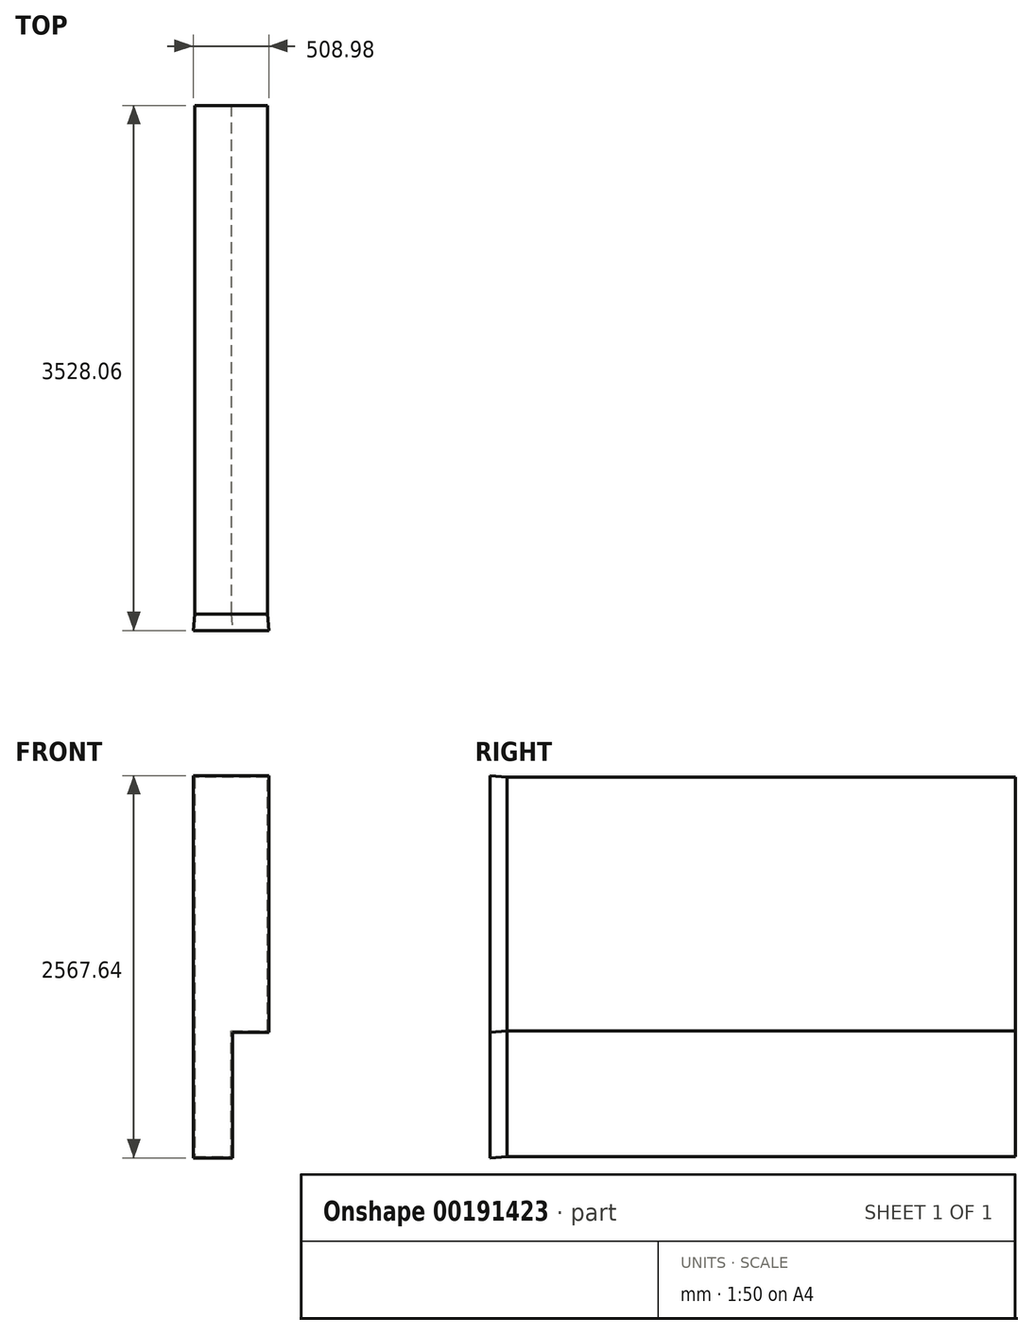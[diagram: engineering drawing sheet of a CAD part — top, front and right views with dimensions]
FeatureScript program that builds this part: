
annotation { "Feature Type Name" : "Feature", "Feature Type Description" : "" }
export const myFeature = defineFeature(function(context is Context, id is Id, definition is map)
    precondition{}
    {
        {
            var Q0;
            Q0=qCreatedBy(makeId("Front.planeOp"),FACE);
            var sketch = newSketch(context, id + "F0", { "sketchPlane" : qUnion([Q0])});
            skLineSegment(sketch, "E0", {"start": v(-244.71, 1274.04) * mm, "end": v(-244.71, -1274.04) * mm});
            skLineSegment(sketch, "E1", {"start": v(-244.71, -1274.04) * mm, "end": v(-0.02, -1274.04) * mm});
            skLineSegment(sketch, "E2", {"start": v(-0.02, -1274.04) * mm, "end": v(-0.02, -430.36) * mm});
            skLineSegment(sketch, "E3", {"start": v(-0.02, -430.36) * mm, "end": v(244.71, -430.36) * mm});
            skLineSegment(sketch, "E4", {"start": v(244.71, -430.36) * mm, "end": v(244.71, 1274.04) * mm});
            skLineSegment(sketch, "E5", {"start": v(244.71, 1274.04) * mm, "end": v(-244.71, 1274.04) * mm});
            skSolve(sketch);
        }
        {
            var Q0;
            Q0=makeQuery(id+"F0.imprint","IMPRINT",FACE,{"disambiguationData":[TD([[makeQuery(id+"F0.imprint","IMPRINT",EDGE,{"derivedFrom":sQuery(id+"F0.wireOp",EDGE,"E0")}),1.0]])]});
            extrude(context, id + "F1", {"entities" : qUnion([Q0]), "oppositeDirection" : true, "depth" : 3416.3 * mm, "hasSecondDirection" : true, "secondDirectionOppositeDirection" : false, "secondDirectionDepth" : 111.76 * mm, "hasSecondDirectionDraft" : true, "secondDirectionDraftAngle" : 5 * degree});
        }
    });
